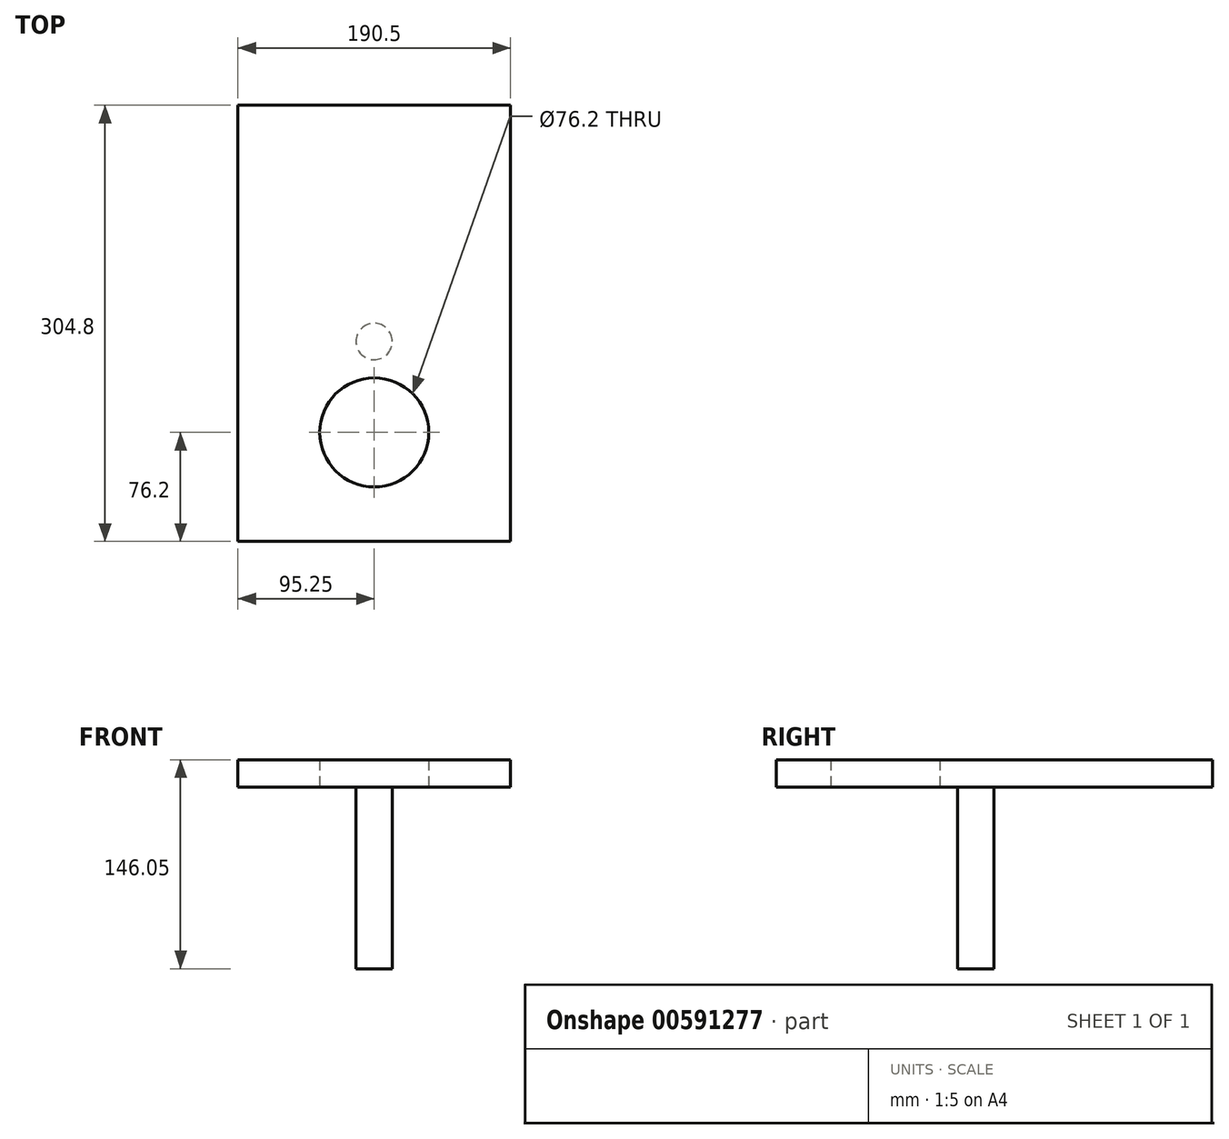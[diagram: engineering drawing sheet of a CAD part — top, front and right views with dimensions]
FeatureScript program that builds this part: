
annotation { "Feature Type Name" : "Feature", "Feature Type Description" : "" }
export const myFeature = defineFeature(function(context is Context, id is Id, definition is map)
    precondition{}
    {
        {
            var Q0;
            Q0=qCreatedBy(makeId("Top.planeOp"),FACE);
            var sketch = newSketch(context, id + "F0", { "sketchPlane" : qUnion([Q0])});
            skLineSegment(sketch, "E0.bottom", {"start": v(95.25, -152.4) * mm, "end": v(-95.25, -152.4) * mm});
            skLineSegment(sketch, "E0.top", {"start": v(95.25, 152.4) * mm, "end": v(-95.25, 152.4) * mm});
            skLineSegment(sketch, "E0.left", {"start": v(95.25, -152.4) * mm, "end": v(95.25, 152.4) * mm});
            skLineSegment(sketch, "E0.right", {"start": v(-95.25, -152.4) * mm, "end": v(-95.25, 152.4) * mm});
            skPoint(sketch, "E0.middle", {"position": v(0, 0) * mm});
            skSolve(sketch);
        }
        {
            var Q0;
            Q0=makeQuery(id+"F0.imprint","IMPRINT",FACE,{"disambiguationData":[TD([[makeQuery(id+"F0.imprint","IMPRINT",EDGE,{"derivedFrom":sQuery(id+"F0.wireOp",EDGE,"E0.bottom")}),-1.0]])]});
            extrude(context, id + "F1", {"entities" : qUnion([Q0]), "depth" : 19.05 * mm, "offsetDistance" : 25.4 * mm});
        }
        {
            var Q0;
            Q0=makeQuery(id+"F1.opExtrude","CAP_FACE",FACE,{"disambiguationData":[OSD([sQuery(id+"F0.wireOp",EDGE,"E0.bottom"),sQuery(id+"F0.wireOp",EDGE,"E0.top"),sQuery(id+"F0.wireOp",EDGE,"E0.left"),sQuery(id+"F0.wireOp",EDGE,"E0.right")])],"isStart":true});
            var sketch = newSketch(context, id + "F2", { "sketchPlane" : qUnion([Q0])});
            skCircle(sketch, "E1", {"center": v(0, 76.2) * mm, "radius": 38.1 * mm});
            skSolve(sketch);
        }
        {
            var Q0;
            Q0=makeQuery(id+"F2.imprint","IMPRINT",FACE,{"disambiguationData":[TD([[makeQuery(id+"F2.imprint","IMPRINT",EDGE,{"derivedFrom":sQuery(id+"F2.wireOp",EDGE,"E1")}),-1.0]])]});
            var sketch = newSketch(context, id + "F3", { "sketchPlane" : qUnion([Q0])});
            skCircle(sketch, "E2", {"center": v(0, 12.7) * mm, "radius": 12.7 * mm});
            skSolve(sketch);
        }
        {
            var Q0;
            Q0=makeQuery(id+"F2.imprint","IMPRINT",FACE,{"disambiguationData":[TD([[makeQuery(id+"F2.imprint","IMPRINT",EDGE,{"derivedFrom":sQuery(id+"F2.wireOp",EDGE,"E1")}),1.0]])]});
            extrude(context, id + "F4", {"entities" : qUnion([Q0]), "operationType" : NewBodyOperationType.REMOVE, "oppositeDirection" : true, "depth" : 25.4 * mm, "offsetDistance" : 25.4 * mm});
        }
        {
            var Q0;
            Q0=makeQuery(id+"F3.imprint","IMPRINT",FACE,{"disambiguationData":[TD([[makeQuery(id+"F3.imprint","IMPRINT",EDGE,{"derivedFrom":sQuery(id+"F3.wireOp",EDGE,"E2")}),1.0]])]});
            extrude(context, id + "F5", {"entities" : qUnion([Q0]), "operationType" : NewBodyOperationType.ADD, "depth" : 127 * mm, "offsetDistance" : 25.4 * mm});
        }
    });
